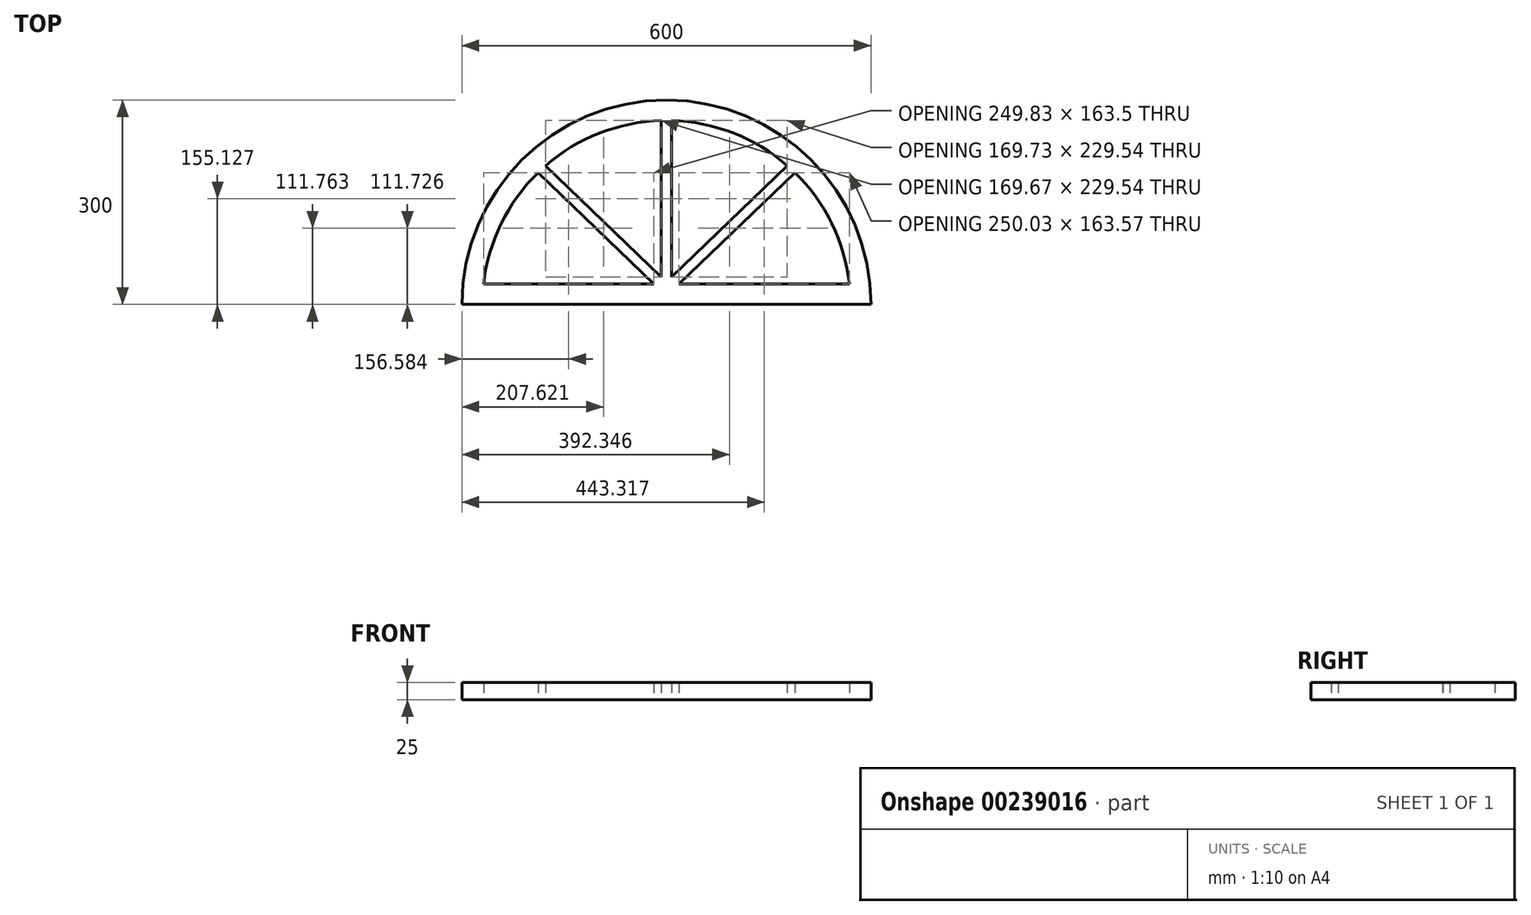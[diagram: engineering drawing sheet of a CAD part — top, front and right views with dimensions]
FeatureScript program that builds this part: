
annotation { "Feature Type Name" : "Feature", "Feature Type Description" : "" }
export const myFeature = defineFeature(function(context is Context, id is Id, definition is map)
    precondition{}
    {
        {
            var Q0;
            Q0=qCreatedBy(makeId("Top.planeOp"),FACE);
            var sketch = newSketch(context, id + "F0", { "sketchPlane" : qUnion([Q0])});
            skArc(sketch, "E0", {"start": v(300, 0) * mm, "mid": v(0, 300) * mm, "end": v(-300, 0) * mm});
            skLineSegment(sketch, "E1", {"start": v(0, 0) * mm, "end": v(300, 0) * mm});
            skLineSegment(sketch, "E2", {"start": v(0, 0) * mm, "end": v(-300, 0) * mm});
            skArc(sketch, "E3", {"start": v(268.33, 29.98) * mm, "mid": v(242.5, 118.72) * mm, "end": v(188.25, 193.55) * mm});
            skLineSegment(sketch, "E4", {"start": v(-268.33, 29.98) * mm, "end": v(-18.5, 29.98) * mm});
            skPoint(sketch, "E5.start.orphan", {"position": v(270, 0) * mm});
            skLineSegment(sketch, "E6", {"start": v(-7.54, 40.36) * mm, "end": v(-7.54, 269.9) * mm});
            skLineSegment(sketch, "E7", {"start": v(7.5, 40.36) * mm, "end": v(7.48, 270) * mm});
            skArc(sketch, "E8.trimOffspring", {"start": v(-7.54, 269.9) * mm, "mid": v(-98.13, 251.54) * mm, "end": v(-177.21, 203.7) * mm});
            skLineSegment(sketch, "E9.trimOffspring", {"start": v(18.3, 29.98) * mm, "end": v(268.33, 29.98) * mm});
            skLineSegment(sketch, "E10", {"start": v(188.25, 193.55) * mm, "end": v(18.3, 29.98) * mm});
            skLineSegment(sketch, "E11", {"start": v(177.21, 203.7) * mm, "end": v(7.5, 40.36) * mm});
            skLineSegment(sketch, "E12", {"start": v(-177.21, 203.7) * mm, "end": v(-7.54, 40.36) * mm});
            skLineSegment(sketch, "E13", {"start": v(-188.4, 193.55) * mm, "end": v(-18.5, 29.98) * mm});
            skPoint(sketch, "E14.start.orphan", {"position": v(0, 29.98) * mm});
            skArc(sketch, "E15.trimOffspring", {"start": v(177.21, 203.7) * mm, "mid": v(98.1, 251.55) * mm, "end": v(7.48, 269.9) * mm});
            skArc(sketch, "E16.trimOffspring", {"start": v(-188.33, 193.48) * mm, "mid": v(-242.52, 118.67) * mm, "end": v(-268.33, 29.98) * mm});
            skPoint(sketch, "E17.start.orphan", {"position": v(-7.54, 29.98) * mm});
            skPoint(sketch, "E18.start.orphan", {"position": v(-182.8, 198.7) * mm});
            skPoint(sketch, "E19.end.orphan", {"position": v(182.8, 198.7) * mm});
            skSolve(sketch);
        }
        {
            var Q0;
            Q0=makeQuery(id+"F0.imprint","IMPRINT",FACE,{"disambiguationData":[TD([[makeQuery(id+"F0.imprint","IMPRINT",EDGE,{"derivedFrom":sQuery(id+"F0.wireOp",EDGE,"E0")}),1.0]])]});
            extrude(context, id + "F1", {"entities" : qUnion([Q0]), "depth" : 25 * mm});
        }
    });
